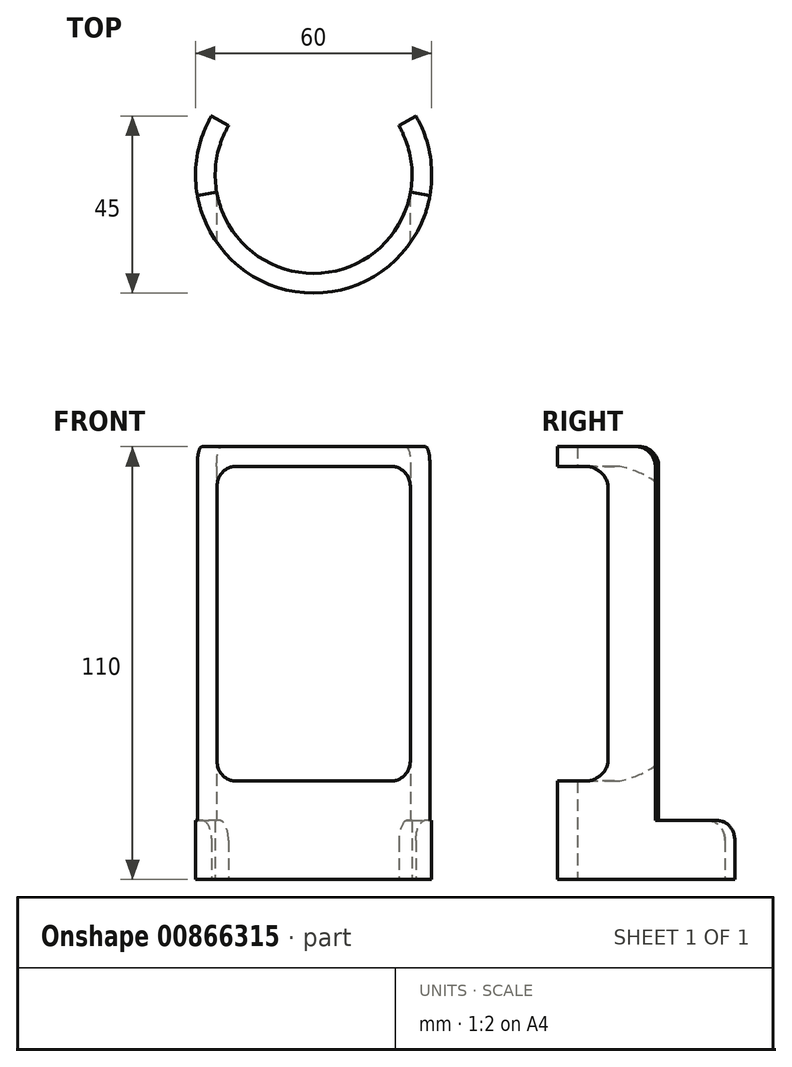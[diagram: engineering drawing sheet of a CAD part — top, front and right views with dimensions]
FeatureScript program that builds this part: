
annotation { "Feature Type Name" : "Feature", "Feature Type Description" : "" }
export const myFeature = defineFeature(function(context is Context, id is Id, definition is map)
    precondition{}
    {
        {
            var Q0;
            Q0=qCreatedBy(makeId("Top.planeOp"),FACE);
            var sketch = newSketch(context, id + "F0", { "sketchPlane" : qUnion([Q0])});
            skCircle(sketch, "E0", {"center": v(0, 0) * mm, "radius": 30 * mm});
            skCircle(sketch, "E1", {"center": v(0, 0) * mm, "radius": 25 * mm});
            skLineSegment(sketch, "E2", {"start": v(-29.54, -5.2) * mm, "end": v(-24.62, -4.34) * mm});
            skLineSegment(sketch, "E3", {"start": v(24.62, -4.34) * mm, "end": v(29.54, -5.2) * mm});
            skLineSegment(sketch, "E4", {"start": v(-21.65, 12.5) * mm, "end": v(-25.98, 15) * mm});
            skLineSegment(sketch, "E5", {"start": v(21.65, 12.5) * mm, "end": v(25.98, 15) * mm});
            skArc(sketch, "E6", {"start": v(-27.08, -4.78) * mm, "mid": v(0, -27.5) * mm, "end": v(27.08, -4.78) * mm});
            skSolve(sketch);
        }
        {
            var Q0;
            {var subQ0=sQuery(id+"F0.wireOp",EDGE,"E2");Q0=makeQuery(id+"F0.imprint","IMPRINT",FACE,{"disambiguationData":[TD([[makeQuery(id+"F0.imprint","IMPRINT",EDGE,{"derivedFrom":subQ0}),1.0]])]});}
            var Q1;
            {var subQ0=sQuery(id+"F0.wireOp",EDGE,"E3");Q1=makeQuery(id+"F0.imprint","IMPRINT",FACE,{"disambiguationData":[TD([[makeQuery(id+"F0.imprint","IMPRINT",EDGE,{"derivedFrom":subQ0}),1.0]])]});}
            extrude(context, id + "F1", {"entities" : qUnion([Q0, Q1]), "depth" : 15 * mm, "offsetDistance" : 25 * mm});
        }
        {
            var Q0;
            {var subQ0=sQuery(id+"F0.wireOp",EDGE,"E2");Q0=makeQuery(id+"F0.imprint","IMPRINT",FACE,{"disambiguationData":[TD([[makeQuery(id+"F0.imprint","IMPRINT",EDGE,{"derivedFrom":subQ0}),-1.0]])]});}
            extrude(context, id + "F2", {"entities" : qUnion([Q0]), "operationType" : NewBodyOperationType.ADD, "depth" : 110 * mm, "offsetDistance" : 25 * mm});
        }
        {
            var Q0;
            Q0=qCreatedBy(makeId("Front.planeOp"),FACE);
            var sketch = newSketch(context, id + "F3", { "sketchPlane" : qUnion([Q0])});
            skLineSegment(sketch, "E7.0", {"start": v(-29.54, 110) * mm, "end": v(29.54, 110) * mm});
            skLineSegment(sketch, "E8.0", {"start": v(-29.54, 110) * mm, "end": v(-29.54, 15) * mm});
            skLineSegment(sketch, "E9.0", {"start": v(29.54, 110) * mm, "end": v(29.54, 15) * mm});
            skLineSegment(sketch, "E10.bottom", {"start": v(-24.54, 105) * mm, "end": v(24.54, 105) * mm});
            skLineSegment(sketch, "E10.top", {"start": v(-24.54, 25) * mm, "end": v(24.54, 25) * mm});
            skLineSegment(sketch, "E10.left", {"start": v(-24.54, 105) * mm, "end": v(-24.54, 25) * mm});
            skLineSegment(sketch, "E10.right", {"start": v(24.54, 105) * mm, "end": v(24.54, 25) * mm});
            skSolve(sketch);
        }
        {
            var Q0;
            Q0=makeQuery(id+"F3.imprint","IMPRINT",FACE,{"disambiguationData":[TD([[makeQuery(id+"F3.imprint","IMPRINT",EDGE,{"derivedFrom":sQuery(id+"F3.wireOp",EDGE,"E10.bottom")}),-1.0]])]});
            extrude(context, id + "F4", {"entities" : qUnion([Q0]), "operationType" : NewBodyOperationType.REMOVE, "depth" : 40 * mm, "offsetDistance" : 25 * mm});
        }
        {
            var Q0;
            Q0=makeQuery(id+"F4.boolean.opBoolean","COPY",EDGE,{"derivedFrom":makeQuery(id+"F4.opExtrude","SWEPT_EDGE",EDGE,{"disambiguationData":[OSD([sQuery(id+"F3.wireOp",EDGE,"E10.top"),sQuery(id+"F3.wireOp",EDGE,"E10.right")])]})});
            var Q1;
            Q1=makeQuery(id+"F4.boolean.opBoolean","COPY",EDGE,{"derivedFrom":makeQuery(id+"F4.opExtrude","SWEPT_EDGE",EDGE,{"disambiguationData":[OSD([sQuery(id+"F3.wireOp",EDGE,"E10.bottom"),sQuery(id+"F3.wireOp",EDGE,"E10.right")])]})});
            var Q2;
            Q2=makeQuery(id+"F4.boolean.opBoolean","COPY",EDGE,{"derivedFrom":makeQuery(id+"F4.opExtrude","SWEPT_EDGE",EDGE,{"disambiguationData":[OSD([sQuery(id+"F3.wireOp",EDGE,"E10.bottom"),sQuery(id+"F3.wireOp",EDGE,"E10.left")])]})});
            var Q3;
            Q3=makeQuery(id+"F2.opExtrude","CAP_EDGE",EDGE,{"disambiguationData":[OSD([sQuery(id+"F0.wireOp",EDGE,"E3")])],"isStart":false});
            var Q4;
            Q4=makeQuery(id+"F2.opExtrude","CAP_EDGE",EDGE,{"disambiguationData":[OSD([sQuery(id+"F0.wireOp",EDGE,"E2")])],"isStart":false});
            var Q5;
            Q5=makeQuery(id+"F4.boolean.opBoolean","COPY",EDGE,{"derivedFrom":makeQuery(id+"F4.opExtrude","SWEPT_EDGE",EDGE,{"disambiguationData":[OSD([sQuery(id+"F3.wireOp",EDGE,"E10.top"),sQuery(id+"F3.wireOp",EDGE,"E10.left")])]})});
            var Q6;
            Q6=makeQuery(id+"F1.opExtrude","CAP_EDGE",EDGE,{"disambiguationData":[OSD([sQuery(id+"F0.wireOp",EDGE,"E3")])],"isStart":false});
            var Q7;
            Q7=makeQuery(id+"F1.opExtrude","CAP_EDGE",EDGE,{"disambiguationData":[OSD([sQuery(id+"F0.wireOp",EDGE,"E5")])],"isStart":false});
            var Q8;
            Q8=makeQuery(id+"F1.opExtrude","CAP_EDGE",EDGE,{"disambiguationData":[OSD([sQuery(id+"F0.wireOp",EDGE,"E4")])],"isStart":false});
            var Q9;
            Q9=makeQuery(id+"F1.opExtrude","CAP_EDGE",EDGE,{"disambiguationData":[OSD([sQuery(id+"F0.wireOp",EDGE,"E2")])],"isStart":false});
            fillet(context, id + "F5", {"entities" : qUnion([Q0, Q1, Q2, Q3, Q4, Q5, Q6, Q7, Q8, Q9]), "radius" : 5 * mm, "tangentPropagation" : true, "allowEdgeOverflow" : false});
        }
    });
